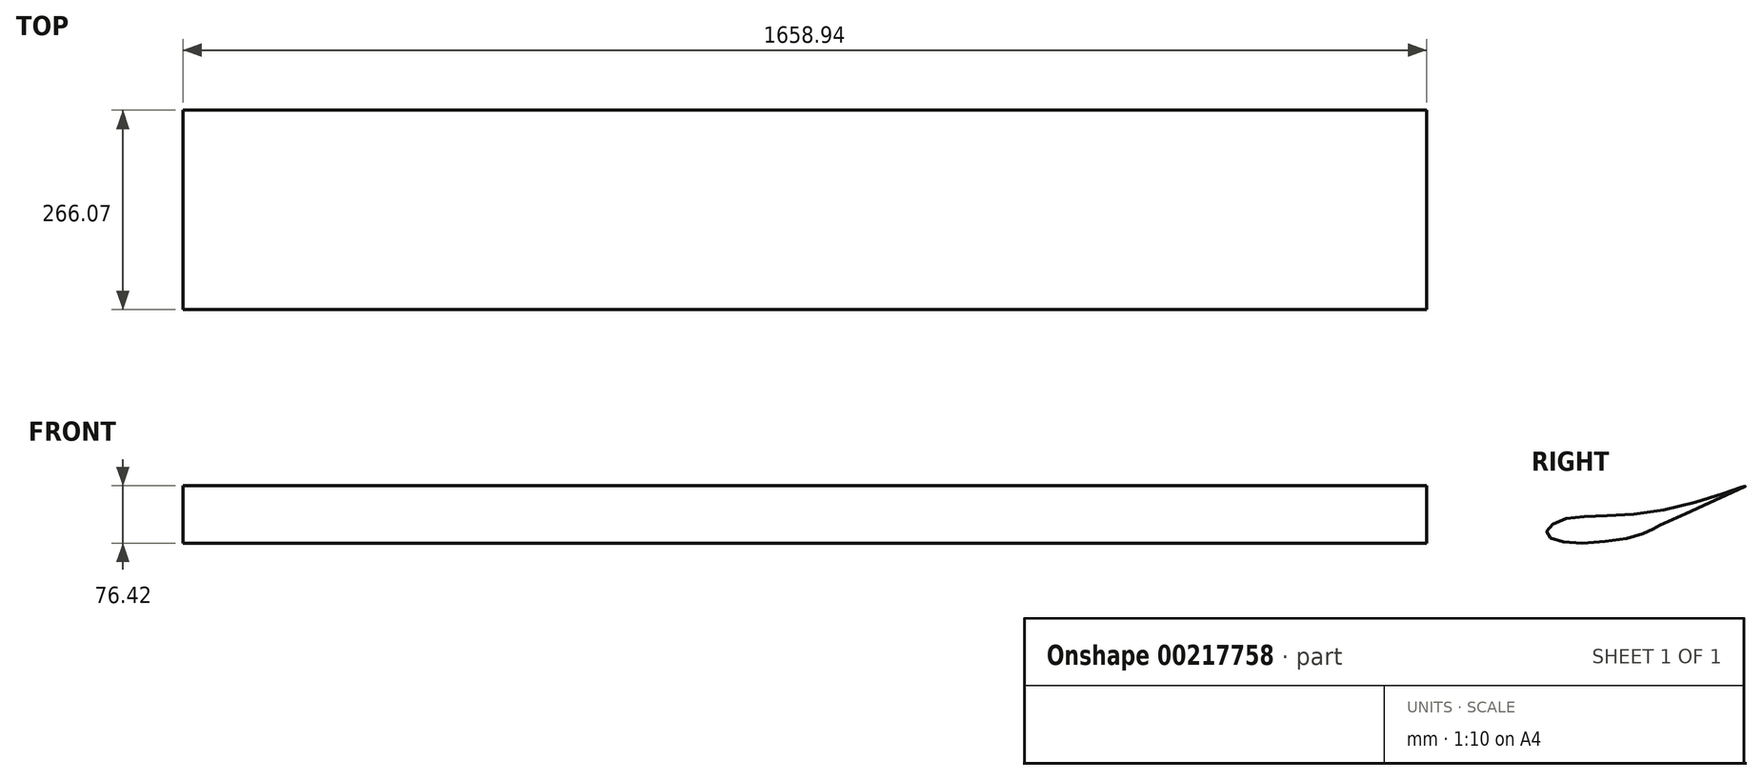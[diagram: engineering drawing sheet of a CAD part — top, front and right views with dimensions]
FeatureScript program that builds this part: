
annotation { "Feature Type Name" : "Feature", "Feature Type Description" : "" }
export const myFeature = defineFeature(function(context is Context, id is Id, definition is map)
    precondition{}
    {
        {
            var Q0;
            Q0=qCreatedBy(makeId("Right.planeOp"),FACE);
            var sketch = newSketch(context, id + "F0", { "sketchPlane" : qUnion([Q0])});
            skFitSpline(sketch, "E0", {"points": [v(-113.42, -12.37) * mm, v(-135.34, 0) * mm, v(-116.2, 17.04) * mm, v(14.34, 28.99) * mm, v(130.5, 62.34) * mm, v(33.94, 18.45) * mm, v(12.13, 8.1) * mm, v(-13.92, -3.67) * mm, v(-113.42, -12.37) * mm]});
            skSolve(sketch);
        }
        {
            var Q0;
            Q0 = qSketchRegion(id + "F0", true);
            extrude(context, id + "F1", {"entities" : qUnion([Q0]), "endBound" : BoundingType.SYMMETRIC, "depth" : 1658.94 * mm});
        }
    });
